# Revit family: IS_ConnectSpace_E0337_BIM_DE
name_source: partatom
category: Plumbing Fixtures
revit_build: Autodesk Revit MEP 2016 (Build: 20161004_0715(x64)
units: mm (PartAtom-declared; Revit-internal decimal feet)

## family parameters
Always vertical = No
Cut with Voids When Loaded = No
OmniClass Number = 23.45.05.14.21.11
OmniClass Title = Bath/Shower Units
Part Type = Normal
Room Calculation Point = No
Round Connector Dimension = Use Diameter
Shared = No
Work Plane-Based = No

## types (5) — shared parameters
Accessories = www.idealstandard.de\ersatzteile
AreaUnits = millimeters
AssetType = Fixed
BIMobject category = Storage
BOSUseNativeGeometries = 1
Brand = Ideal Standard
Brand url = http://www.idealstandard.co.uk
ConnectionType = Mechanical
CurrencyUnit = €
Date of publishing = 06/11/2017
DurationUnit = year
EAN code = https://5017830454465
Edition number = 1
ExpectedLife = 25
Features = CONNECT SPACE vanity unit 490x375mm, 1 drawer
IFC Classification = Sanitary Terminal
IfcExportAs = Sanitary Terminal Type
IfcExportType = VanityUnits
Installation instructions = http://www.idealstandard.de
InstallationInstructions = www.idealstandard.de\produkte
LinearUnits = millimeters
MaintenanceInformation = www.idealstandard.de\produkte
Manufacturer name = Ideal Standard
ManufacturerURL = www.idealstandard.com
ModelReference = CONNECT SPACE vanity unit 490x375mm, 1 drawer
NBS Reference Code = 35-75-94
NBS Reference Description = Vanity Units
Nominal height = 513
Nominal width = 490
NominalDepth = 396 mm  [stored 1.29921 ft]
NominalHeight = 513 mm  [stored 1.68307 ft]
NominalLength = 396 mm  [stored 1.29921 ft]
NominalWidth = 490 mm  [stored 1.60761 ft]
Product Guid = 0ecd5f54-629f-427c-bcb6-8663a990eab6
Product SKU = E0337
Product data url = https://bimobject.com
Product family = CONNECT SPACE
Product group = Furniture
Product name = CONNECT SPACE vanity unit 490x375mm, 1 drawer
Product url = http://www.idealstandard.de
ProductInformation = www.idealstandard.de/produkte
QR code = http://bimobject.com
Shape = Rectangular
Size = 490x396x513 mm
Space = Internal
SpareParts = www.idealstandard.de/ersatzteile
Technical description = http://www.idealstandard.de
URL = www.idealstandard.com
Uniclass 2.0 Code = PR-35-75-94
Uniclass 2.0 Description = Vanity Units
Uniclass 2015 Code = Pr_40_20_76_94
Uniclass 2015 Name = Vanity units
Uniclass2015Code = Pr_40_20_76_94
Uniclass2015Title = Vanity units
Uniclass2015Version = Products v1.1
Version = 1
VolumeUnits = Litres
Weight Net (Kg) = 20

## per-type parameters (varying)
| type | BIMObjectName | BarCode | Color | Finish | MainColor | Model | ModelNumber | Name | NettWeight |
| E0337WG CONNECT SPACE vanity unit 490x375mm, 1 drawer | ISI_IdealStandard_Furniture_Connect Space_E0337WG | 5017830454465 | Glossy White | Glossy White | Glossy White | E0337WG | E0337WG | Furniture_Connect Space_E0337WG_IdealStandard | 20 kg |
| E0337SO CONNECT SPACE vanity unit 490x375mm, 1 drawer | ISI_IdealStandard_Furniture_Connect Space_E0337SO | 5017830454458 | American  Oak | American  Oak | American  Oak | E0337SO | E0337SO | Furniture_Connect Space_E0337SO_IdealStandard | 20 kg |
| E0337KR CONNECT SPACE vanity unit 490x375mm, 1 drawer | ISI_IdealStandard_Furniture_Connect Space_E0337KR | 5017830454434 | Glossy grey | Glossy grey | Glossy grey | E0337KR | E0337KR | Furniture_Connect Space_E0337KR_IdealStandard | 20,5 kg |
| E0337DK CONNECT SPACE vanity unit 490x375mm, 1 drawer | ISI_IdealStandard_Furniture_Connect Space_E0337DK | 5017830454427 | Walnut | Walnut | Walnut | E0337DK | E0337DK | Furniture_Connect Space_E0337DK_IdealStandard | 20 kg |
| E0337KS CONNECT SPACE vanity unit 490x375mm, 1 drawer | ISI_IdealStandard_Furniture_Connect Space_E0337KS | 5017830454441 | Elm | Elm | Elm | E0337KS | E0337KS | Furniture_Connect Space_E0337KS_IdealStandard | 20 kg |

note: column(s) folded — value = type name in every type: Description

note: [stored X ft] marks values corroborated as IEEE doubles in the binary element streams (Revit-internal decimal feet)

## geometry (parser evidence)
native form markers: Blend x2, Sweep x1
no freeform markers — native parametric forms only
